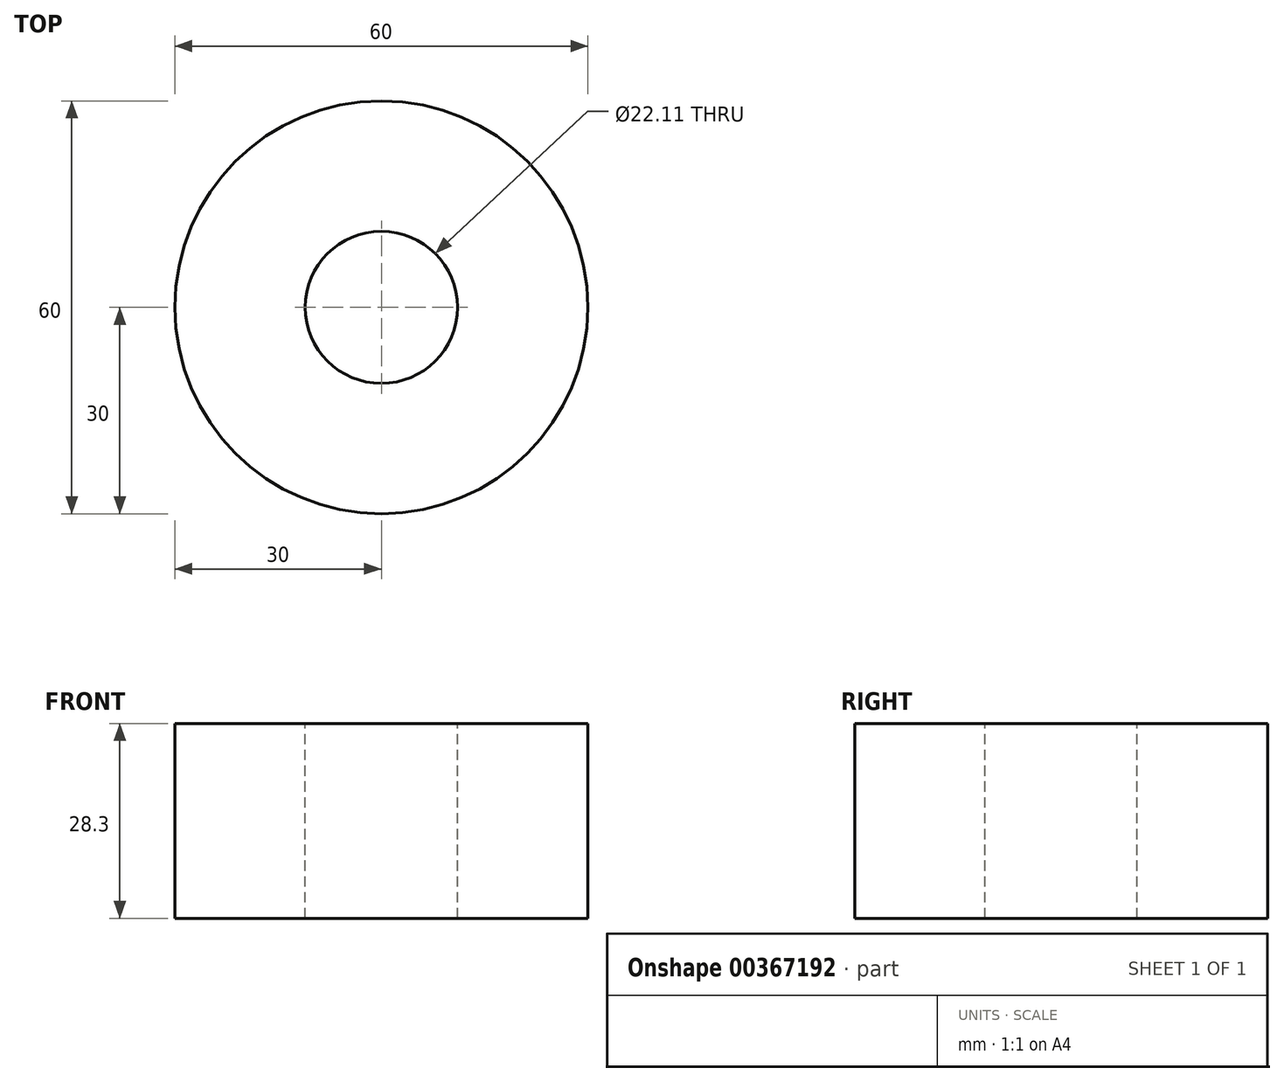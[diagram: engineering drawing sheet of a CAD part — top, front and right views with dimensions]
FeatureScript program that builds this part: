
annotation { "Feature Type Name" : "Feature", "Feature Type Description" : "" }
export const myFeature = defineFeature(function(context is Context, id is Id, definition is map)
    precondition{}
    {
        {
            var Q0;
            Q0=qCreatedBy(makeId("Front.planeOp"),FACE);
            var sketch = newSketch(context, id + "F0", { "sketchPlane" : qUnion([Q0])});
            skLineSegment(sketch, "E0.bottom", {"start": v(0, 0) * mm, "end": v(30, 0) * mm});
            skLineSegment(sketch, "E0.top", {"start": v(0, -28.3) * mm, "end": v(30, -28.3) * mm});
            skLineSegment(sketch, "E0.left", {"start": v(0, 0) * mm, "end": v(0, -28.3) * mm});
            skLineSegment(sketch, "E0.right", {"start": v(30, 0) * mm, "end": v(30, -28.3) * mm});
            skSolve(sketch);
        }
        {
            var Q0;
            Q0=makeQuery(id+"F0.imprint","IMPRINT",FACE,{"disambiguationData":[TD([[makeQuery(id+"F0.imprint","IMPRINT",EDGE,{"derivedFrom":sQuery(id+"F0.wireOp",EDGE,"E0.bottom")}),-1.0]])]});
            var Q1;
            Q1=sQuery(id+"F0.wireOp",EDGE,"E0.right");
            revolve(context, id + "F1", {"entities" : qUnion([Q0]), "axis" : qUnion([Q1]), "revolveType" : RevolveType.FULL});
        }
        {
            var Q0;
            Q0=makeQuery(id+"F1.opRevolve","SWEPT_FACE",FACE,{"disambiguationData":[OSD([sQuery(id+"F0.wireOp",EDGE,"E0.bottom")])]});
            var sketch = newSketch(context, id + "F2", { "sketchPlane" : qUnion([Q0])});
            skCircle(sketch, "E1", {"center": v(30, 0) * mm, "radius": 11.06 * mm});
            skSolve(sketch);
        }
        {
            var Q0;
            Q0 = qSketchRegion(id + "F2", true);
            extrude(context, id + "F3", {"entities" : qUnion([Q0]), "operationType" : NewBodyOperationType.REMOVE, "oppositeDirection" : true, "depth" : 40 * mm});
        }
    });
